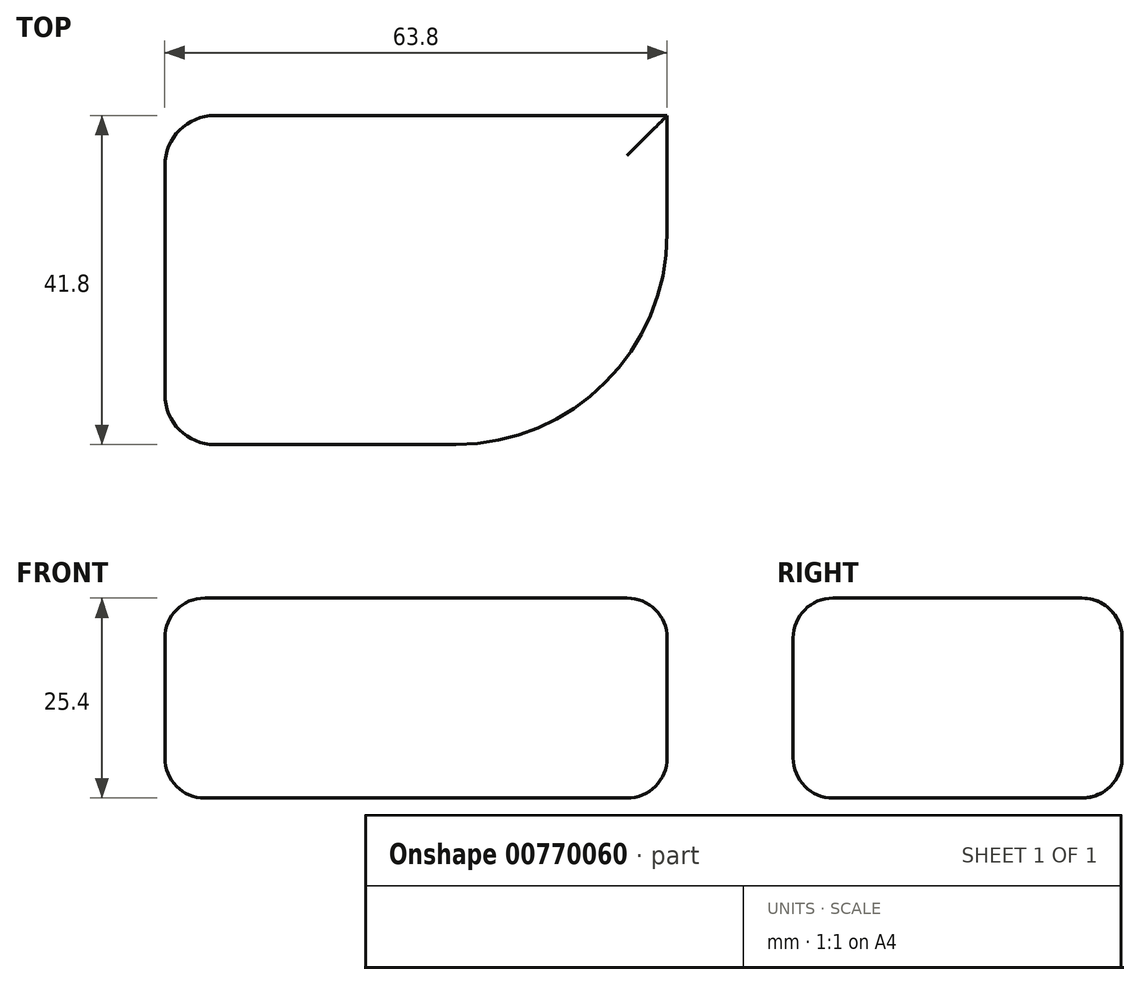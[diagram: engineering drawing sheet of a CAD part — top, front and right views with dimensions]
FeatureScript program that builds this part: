
annotation { "Feature Type Name" : "Feature", "Feature Type Description" : "" }
export const myFeature = defineFeature(function(context is Context, id is Id, definition is map)
    precondition{}
    {
        {
            var Q0;
            Q0=qCreatedBy(makeId("Top.planeOp"),FACE);
            var sketch = newSketch(context, id + "F0", { "sketchPlane" : qUnion([Q0])});
            skLineSegment(sketch, "E0.bottom", {"start": v(31.9, 20.9) * mm, "end": v(-25.55, 20.9) * mm});
            skLineSegment(sketch, "E0.top", {"start": v(5.07, -20.9) * mm, "end": v(-25.55, -20.9) * mm});
            skLineSegment(sketch, "E0.left", {"start": v(31.9, 20.9) * mm, "end": v(31.9, 5.93) * mm});
            skLineSegment(sketch, "E0.right", {"start": v(-31.9, 14.55) * mm, "end": v(-31.9, -14.55) * mm});
            skPoint(sketch, "E0.middle", {"position": v(0, 0) * mm});
            skPoint(sketch, "E1.visualSharp", {"position": v(-31.9, 20.9) * mm});
            skArc(sketch, "E1.filletArc", {"start": v(-25.55, 20.9) * mm, "mid": v(-30.04, 19.04) * mm, "end": v(-31.9, 14.55) * mm});
            skPoint(sketch, "E2.visualSharp", {"position": v(-31.9, -20.9) * mm});
            skArc(sketch, "E2.filletArc", {"start": v(-31.9, -14.55) * mm, "mid": v(-30.04, -19.04) * mm, "end": v(-25.55, -20.9) * mm});
            skPoint(sketch, "E3.visualSharp", {"position": v(31.9, -20.9) * mm});
            skArc(sketch, "E3.filletArc", {"start": v(5.07, -20.9) * mm, "mid": v(24.04, -13.04) * mm, "end": v(31.9, 5.93) * mm});
            skSolve(sketch);
        }
        {
            var Q0;
            Q0=makeQuery(id+"F0.imprint","IMPRINT",FACE,{"disambiguationData":[TD([[makeQuery(id+"F0.imprint","IMPRINT",EDGE,{"derivedFrom":sQuery(id+"F0.wireOp",EDGE,"E0.bottom")}),1.0]])]});
            extrude(context, id + "F1", {"entities" : qUnion([Q0]), "depth" : 25.4 * mm, "offsetDistance" : 25.4 * mm});
        }
        {
            var Q0;
            Q0=makeQuery(id+"F1.opExtrude","CAP_EDGE",EDGE,{"disambiguationData":[OSD([sQuery(id+"F0.wireOp",EDGE,"E3.filletArc")])],"isStart":false});
            var Q1;
            Q1=makeQuery(id+"F1.opExtrude","CAP_EDGE",EDGE,{"disambiguationData":[OSD([sQuery(id+"F0.wireOp",EDGE,"E0.left")])],"isStart":false});
            var Q2;
            Q2=makeQuery(id+"F1.opExtrude","CAP_EDGE",EDGE,{"disambiguationData":[OSD([sQuery(id+"F0.wireOp",EDGE,"E0.bottom")])],"isStart":false});
            var Q3;
            Q3=makeQuery(id+"F1.opExtrude","CAP_EDGE",EDGE,{"disambiguationData":[OSD([sQuery(id+"F0.wireOp",EDGE,"E1.filletArc")])],"isStart":false});
            var Q4;
            Q4=makeQuery(id+"F1.opExtrude","CAP_EDGE",EDGE,{"disambiguationData":[OSD([sQuery(id+"F0.wireOp",EDGE,"E0.right")])],"isStart":false});
            var Q5;
            Q5=makeQuery(id+"F1.opExtrude","CAP_EDGE",EDGE,{"disambiguationData":[OSD([sQuery(id+"F0.wireOp",EDGE,"E0.top")])],"isStart":false});
            var Q6;
            Q6=makeQuery(id+"F1.opExtrude","CAP_EDGE",EDGE,{"disambiguationData":[OSD([sQuery(id+"F0.wireOp",EDGE,"E2.filletArc")])],"isStart":false});
            fillet(context, id + "F2", {"entities" : qUnion([Q0, Q1, Q2, Q3, Q4, Q5, Q6]), "radius" : 5.08 * mm, "tangentPropagation" : true, "allowEdgeOverflow" : false});
        }
        {
            var Q0;
            Q0=makeQuery(id+"F1.opExtrude","CAP_EDGE",EDGE,{"disambiguationData":[OSD([sQuery(id+"F0.wireOp",EDGE,"E0.bottom")])],"isStart":true});
            var Q1;
            Q1=makeQuery(id+"F1.opExtrude","CAP_EDGE",EDGE,{"disambiguationData":[OSD([sQuery(id+"F0.wireOp",EDGE,"E0.left")])],"isStart":true});
            var Q2;
            Q2=makeQuery(id+"F1.opExtrude","CAP_EDGE",EDGE,{"disambiguationData":[OSD([sQuery(id+"F0.wireOp",EDGE,"E3.filletArc")])],"isStart":true});
            var Q3;
            Q3=makeQuery(id+"F1.opExtrude","CAP_EDGE",EDGE,{"disambiguationData":[OSD([sQuery(id+"F0.wireOp",EDGE,"E0.top")])],"isStart":true});
            var Q4;
            Q4=makeQuery(id+"F1.opExtrude","CAP_EDGE",EDGE,{"disambiguationData":[OSD([sQuery(id+"F0.wireOp",EDGE,"E2.filletArc")])],"isStart":true});
            var Q5;
            Q5=makeQuery(id+"F1.opExtrude","CAP_EDGE",EDGE,{"disambiguationData":[OSD([sQuery(id+"F0.wireOp",EDGE,"E0.right")])],"isStart":true});
            var Q6;
            Q6=makeQuery(id+"F1.opExtrude","CAP_EDGE",EDGE,{"disambiguationData":[OSD([sQuery(id+"F0.wireOp",EDGE,"E1.filletArc")])],"isStart":true});
            fillet(context, id + "F3", {"entities" : qUnion([Q0, Q1, Q2, Q3, Q4, Q5, Q6]), "radius" : 5.08 * mm, "tangentPropagation" : true, "allowEdgeOverflow" : false});
        }
    });
